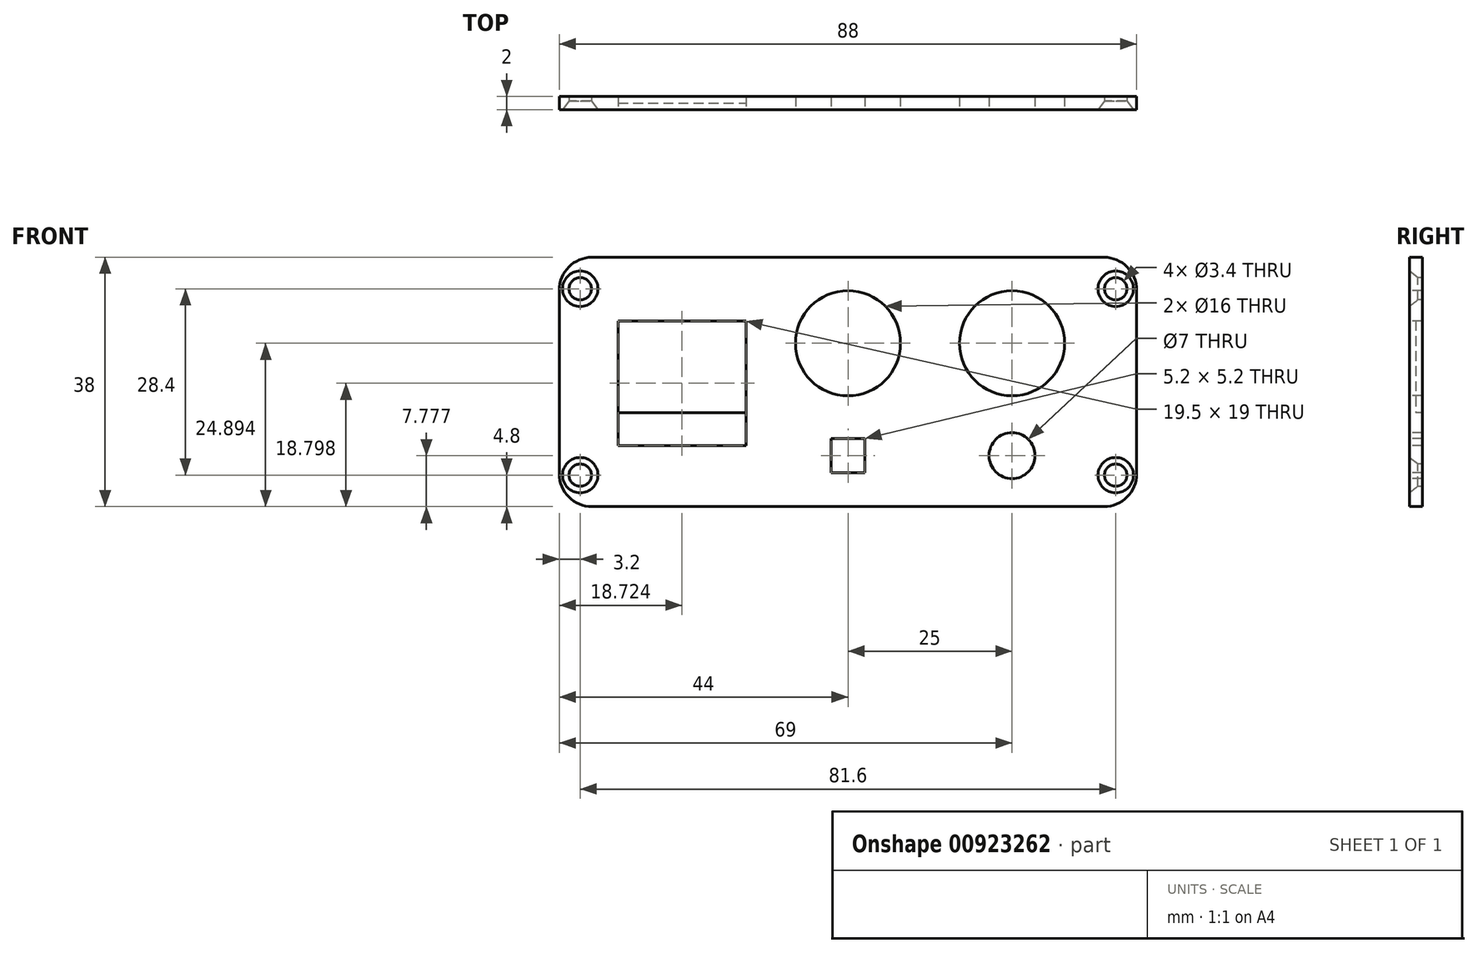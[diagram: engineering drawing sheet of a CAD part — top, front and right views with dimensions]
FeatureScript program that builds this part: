
annotation { "Feature Type Name" : "Feature", "Feature Type Description" : "" }
export const myFeature = defineFeature(function(context is Context, id is Id, definition is map)
    precondition{}
    {
        {
            var Q0;
            Q0=qCreatedBy(makeId("Front.planeOp"),FACE);
            var sketch = newSketch(context, id + "F0", { "sketchPlane" : qUnion([Q0])});
            skLineSegment(sketch, "E0.bottom", {"start": v(-88, 38) * mm, "end": v(0, 38) * mm});
            skLineSegment(sketch, "E0.top", {"start": v(-88, 0) * mm, "end": v(0, 0) * mm});
            skLineSegment(sketch, "E0.left", {"start": v(-88, 38) * mm, "end": v(-88, 0) * mm});
            skLineSegment(sketch, "E0.right", {"start": v(0, 38) * mm, "end": v(0, 0) * mm});
            skCircle(sketch, "E1", {"center": v(-84.8, 33.2) * mm, "radius": 1.7 * mm});
            skLineSegment(sketch, "E2", {"start": v(-84.8, 31.5) * mm, "end": v(-84.8, 6.5) * mm, "construction": true});
            skLineSegment(sketch, "E3", {"start": v(-84.8, 19) * mm, "end": v(0, 19) * mm, "construction": true});
            skCircle(sketch, "E4", {"center": v(-84.8, 4.8) * mm, "radius": 1.7 * mm});
            skLineSegment(sketch, "E5", {"start": v(-44, 38) * mm, "end": v(-44, 0) * mm, "construction": true});
            skCircle(sketch, "E6.MirrorC", {"center": v(-3.2, 33.2) * mm, "radius": 1.7 * mm});
            skLineSegment(sketch, "E7.MirrorCS", {"start": v(-3.2, 31.5) * mm, "end": v(-3.2, 6.5) * mm, "construction": true});
            skCircle(sketch, "E8.MirrorC", {"center": v(-3.2, 4.8) * mm, "radius": 1.7 * mm});
            skPoint(sketch, "E9.middle", {"position": v(-44, 19) * mm});
            skLineSegment(sketch, "E10.bottom", {"start": v(-79.03, 28.3) * mm, "end": v(-59.53, 28.3) * mm});
            skLineSegment(sketch, "E10.top", {"start": v(-79.03, 9.3) * mm, "end": v(-59.53, 9.3) * mm});
            skLineSegment(sketch, "E10.left", {"start": v(-79.03, 28.3) * mm, "end": v(-79.03, 9.3) * mm});
            skLineSegment(sketch, "E10.right", {"start": v(-59.53, 28.3) * mm, "end": v(-59.53, 9.3) * mm});
            skCircle(sketch, "E11", {"center": v(-19, 7.78) * mm, "radius": 3.5 * mm});
            skCircle(sketch, "E12", {"center": v(-44, 24.9) * mm, "radius": 8 * mm});
            skCircle(sketch, "E13", {"center": v(-19, 24.9) * mm, "radius": 8 * mm});
            skLineSegment(sketch, "E14", {"start": v(-44, 24.9) * mm, "end": v(-19, 24.9) * mm, "construction": true});
            skLineSegment(sketch, "E15", {"start": v(-44, 24.9) * mm, "end": v(-44, 7.78) * mm, "construction": true});
            skLineSegment(sketch, "E16.bottom", {"start": v(-41.4, 5.18) * mm, "end": v(-46.6, 5.18) * mm});
            skLineSegment(sketch, "E16.top", {"start": v(-41.4, 10.38) * mm, "end": v(-46.6, 10.38) * mm});
            skLineSegment(sketch, "E16.left", {"start": v(-41.4, 5.18) * mm, "end": v(-41.4, 10.38) * mm});
            skLineSegment(sketch, "E16.right", {"start": v(-46.6, 5.18) * mm, "end": v(-46.6, 10.38) * mm});
            skPoint(sketch, "E16.middle", {"position": v(-44, 7.78) * mm});
            skLineSegment(sketch, "E17", {"start": v(-79.03, 14.3) * mm, "end": v(-59.53, 14.3) * mm});
            skSolve(sketch);
        }
        {
            var Q0;
            Q0 = qSketchRegion(id + "F0", true);
            extrude(context, id + "F1", {"entities" : qUnion([Q0]), "oppositeDirection" : true, "depth" : 2 * mm, "offsetDistance" : 25 * mm});
        }
        {
            var Q0;
            Q0=makeQuery(id+"F1.opExtrude","SWEPT_EDGE",EDGE,{"disambiguationData":[OSD([sQuery(id+"F0.wireOp",EDGE,"E0.bottom"),sQuery(id+"F0.wireOp",EDGE,"E0.left")])]});
            var Q1;
            Q1=makeQuery(id+"F1.opExtrude","SWEPT_EDGE",EDGE,{"disambiguationData":[OSD([sQuery(id+"F0.wireOp",EDGE,"E0.top"),sQuery(id+"F0.wireOp",EDGE,"E0.left")])]});
            var Q2;
            Q2=makeQuery(id+"F1.opExtrude","SWEPT_EDGE",EDGE,{"disambiguationData":[OSD([sQuery(id+"F0.wireOp",EDGE,"E0.top"),sQuery(id+"F0.wireOp",EDGE,"E0.right")])]});
            var Q3;
            Q3=makeQuery(id+"F1.opExtrude","SWEPT_EDGE",EDGE,{"disambiguationData":[OSD([sQuery(id+"F0.wireOp",EDGE,"E0.bottom"),sQuery(id+"F0.wireOp",EDGE,"E0.right")])]});
            fillet(context, id + "F2", {"entities" : qUnion([Q0, Q1, Q2, Q3]), "radius" : 5 * mm, "tangentPropagation" : true, "allowEdgeOverflow" : false});
        }
        {
            var Q0;
            Q0=sQuery(id+"F0.wireOp",VERTEX,"E4.center");
            var Q1;
            Q1=sQuery(id+"F0.wireOp",VERTEX,"E1.center");
            var Q2;
            Q2=sQuery(id+"F0.wireOp",VERTEX,"E8.MirrorC.center");
            var Q3;
            Q3=sQuery(id+"F0.wireOp",VERTEX,"E6.MirrorC.center");
            var Q4;
            Q4=makeQuery(id+"F1.opExtrude","SWEPT_BODY",BODY,{"disambiguationData":[OSD([sQuery(id+"F0.wireOp",EDGE,"E0.bottom"),sQuery(id+"F0.wireOp",EDGE,"E0.top"),sQuery(id+"F0.wireOp",EDGE,"E0.left"),sQuery(id+"F0.wireOp",EDGE,"E0.right"),sQuery(id+"F0.wireOp",EDGE,"E4"),sQuery(id+"F0.wireOp",EDGE,"E1"),sQuery(id+"F0.wireOp",EDGE,"E6.MirrorC"),sQuery(id+"F0.wireOp",EDGE,"E8.MirrorC"),sQuery(id+"F0.wireOp",EDGE,"E10.bottom"),sQuery(id+"F0.wireOp",EDGE,"E10.top"),sQuery(id+"F0.wireOp",EDGE,"E10.left"),sQuery(id+"F0.wireOp",EDGE,"E10.right"),sQuery(id+"F0.wireOp",EDGE,"E11"),sQuery(id+"F0.wireOp",EDGE,"E12"),sQuery(id+"F0.wireOp",EDGE,"E13"),sQuery(id+"F0.wireOp",EDGE,"E16.bottom"),sQuery(id+"F0.wireOp",EDGE,"E16.top"),sQuery(id+"F0.wireOp",EDGE,"E16.left"),sQuery(id+"F0.wireOp",EDGE,"E16.right")])]});
            hole(context, id + "F3", {"style" : HoleStyle.C_SINK, "endStyle" : HoleEndStyle.BLIND, "holeDiameter" : 3 * mm, "cSinkDiameter" : 5.4 * mm, "cSinkAngle" : 75 * degree, "majorDiameter" : 3 * mm, "holeDepth" : 13.5 * mm, "isTappedThrough" : true, "tappedDepth" : 12 * mm, "tapClearance" : 3, "locations" : qUnion([Q0, Q1, Q2, Q3]), "scope" : qUnion([Q4])});
        }
        {
            var Q0;
            {var subQ0=sQuery(id+"F0.wireOp",EDGE,"E10.bottom");Q0=makeQuery(id+"F0.imprint","IMPRINT",FACE,{"disambiguationData":[TD([[makeQuery(id+"F0.imprint","IMPRINT",EDGE,{"derivedFrom":subQ0}),-1.0]])]});}
            extrude(context, id + "F4", {"entities" : qUnion([Q0]), "oppositeDirection" : true, "depth" : 2 * mm, "offsetDistance" : 25 * mm});
        }
        {
            var Q0;
            {var subQ0=sQuery(id+"F0.wireOp",EDGE,"E10.bottom");Q0=makeQuery(id+"F0.imprint","IMPRINT",FACE,{"disambiguationData":[TD([[makeQuery(id+"F0.imprint","IMPRINT",EDGE,{"derivedFrom":subQ0}),-1.0]])]});}
            extrude(context, id + "F5", {"entities" : qUnion([Q0]), "operationType" : NewBodyOperationType.REMOVE, "oppositeDirection" : true, "depth" : 1 * mm, "offsetDistance" : 25 * mm});
        }
    });
